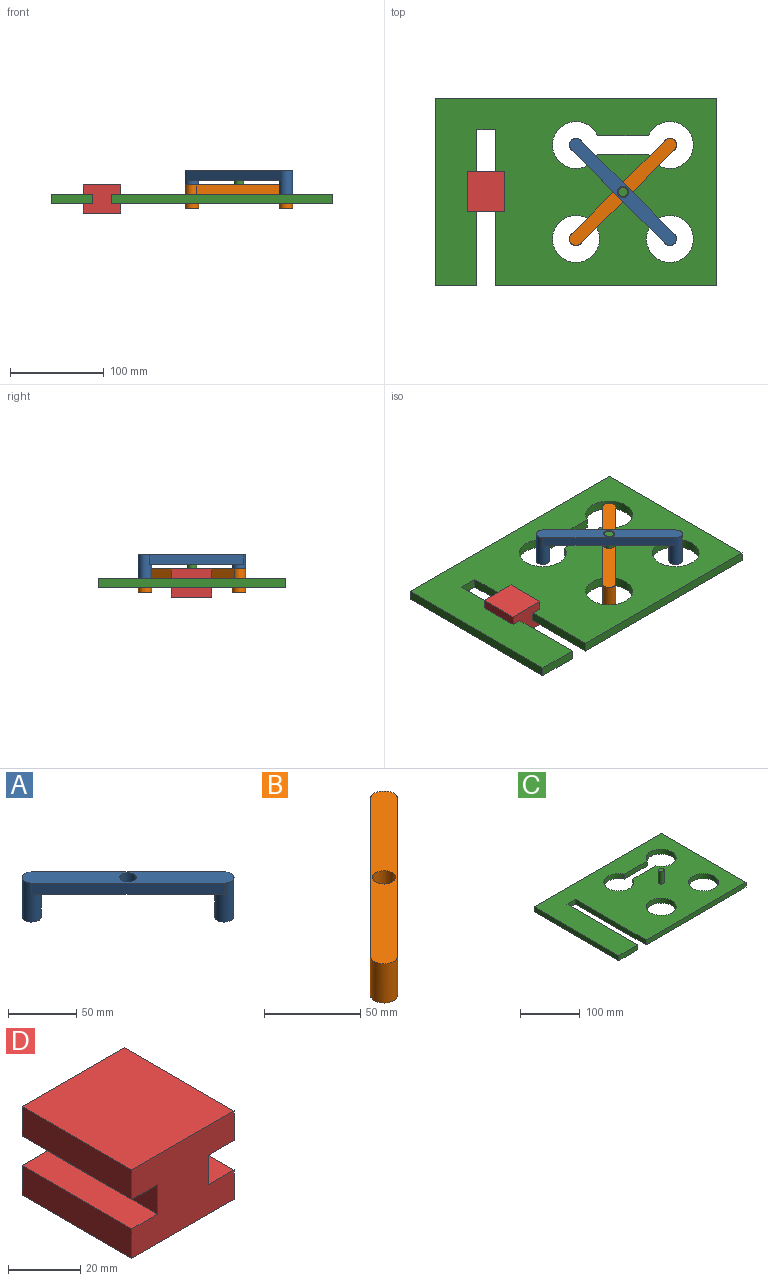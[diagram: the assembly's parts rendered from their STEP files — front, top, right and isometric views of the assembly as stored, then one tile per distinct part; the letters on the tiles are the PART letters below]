
ASSEMBLY  parts=4 mates=3
PART A: 9 faces, bbox 114.1x114.1x35 mm
  f0: cylinder r=7.07mm len=35mm, axis (0,0,1), area 1332.9mm2, adj f1,f3,f5,f6,f7
  f1: plane 100x100mm, normal (-0.71,-0.71,0), area 1414.2mm2, adj f0,f2,f5,f6
  f2: cylinder r=7.07mm len=35mm, axis (0,0,1), area 1332.9mm2, adj f1,f3,f5,f6,f8
  f3: plane 100x100mm, normal (0.71,0.71,0), area 1414.2mm2, adj f0,f2,f5,f6
  f4: cylinder r=6mm len=12mm, axis (0,0,1), area 377mm2, adj f5,f6
  f5: plane 110x110mm, normal (0,0,-1), area 1729.8mm2, adj f0,f1,f2,f3,f4
  f6: plane 114.14x114.14mm, normal (0,0,1), area 2044mm2, adj f0,f1,f2,f3,f4
  f7: plane 14.14x14.14mm, normal (0,0,-1), area 157.1mm2, adj f0
  f8: plane 14.14x14.14mm, normal (0,0,-1), area 157.1mm2, adj f2
PART B: 9 faces, bbox 114.1x114.1x25 mm
  f0: plane 110x110mm, normal (0,0,-1), area 1729.8mm2, adj f1,f2,f3,f4,f5
  f1: plane 100x100mm, normal (0.71,-0.71,0), area 1414.2mm2, adj f0,f2,f4,f6
  f2: cylinder r=7.07mm len=25mm, axis (0,0,-1), area 888.6mm2, adj f0,f1,f3,f6,f8
  f3: plane 100x100mm, normal (-0.71,0.71,0), area 1414.2mm2, adj f0,f2,f4,f6
  f4: cylinder r=7.07mm len=25mm, axis (0,0,-1), area 888.6mm2, adj f0,f1,f3,f6,f7
  f5: cylinder r=6mm len=12mm, axis (0,0,-1), area 377mm2, adj f0,f6
  f6: plane 114.14x114.14mm, normal (0,0,1), area 2044mm2, adj f1,f2,f3,f4,f5
  f7: plane 14.14x14.14mm, normal (0,0,-1), area 157.1mm2, adj f4
  f8: plane 14.14x14.14mm, normal (0,0,-1), area 157.1mm2, adj f2
PART C: 18 faces, bbox 300x200x35 mm
  f0: plane 166.53x10mm, normal (1,0,0), area 1665.3mm2, adj f1,f13,f14,f15
  f1: plane 20x10mm, normal (0,-1,0), area 200mm2, adj f0,f2,f14,f15
  f2: plane 166.53x10mm, normal (-1,0,0), area 1665.3mm2, adj f1,f3,f14,f15
  f3: plane 235.65x10mm, normal (0,-1,0), area 2356.5mm2, adj f2,f4,f14,f15
  f4: plane 200x10mm, normal (1,0,0), area 2000mm2, adj f3,f5,f14,f15
  f5: plane 300x10mm, normal (0,1,0), area 3000mm2, adj f4,f6,f14,f15
  f6: plane 200x10mm, normal (-1,0,0), area 2000mm2, adj f5,f13,f14,f15
  f7: plane 54.17x10mm, normal (0,1,0), area 541.7mm2, adj f8,f10,f14,f15
  f8: cylinder r=25mm len=50mm, axis (0,0,1), area 1365mm2, adj f7,f9,f14,f15
  f9: plane 54.17x10mm, normal (0,-1,0), area 541.7mm2, adj f8,f10,f14,f15
  f10: cylinder r=25mm len=50mm, axis (0,0,1), area 1365mm2, adj f7,f9,f14,f15
  f11: cylinder r=25mm len=50mm, axis (0,0,1), area 1570.8mm2, adj f14,f15
  f12: cylinder r=25mm len=50mm, axis (0,0,1), area 1570.8mm2, adj f14,f15
  f13: plane 44.35x10mm, normal (0,-1,0), area 443.5mm2, adj f0,f6,f14,f15
  f14: plane 300x200mm, normal (0,0,-1), area 47788.1mm2, adj f0,f1,f2,f3,f4,f5,f6,f7
  f15: plane 300x200mm, normal (0,0,1), area 47709.6mm2, adj f0,f1,f2,f3,f4,f5,f6,f7
  f16: cylinder r=5mm len=25mm, axis (0,0,-1), area 785.4mm2, adj f15,f17
  f17: plane 10x10mm, normal (0,0,1), area 78.5mm2, adj f16
PART D: 14 faces, bbox 40x43x30 mm
  f0: plane 43x10mm, normal (0,0,-1), area 430mm2, adj f1,f3,f6,f13
  f1: plane 43x10mm, normal (-1,0,0), area 430mm2, adj f0,f3,f4,f13
  f2: plane 43x10mm, normal (1,0,0), area 430mm2, adj f3,f4,f5,f13
  f3: plane 40x30mm, normal (0,1,0), area 1000mm2, adj f0,f1,f2,f4,f5,f6,f7,f8
  f4: plane 43x40mm, normal (0,0,1), area 1720mm2, adj f1,f2,f3,f13
  f5: plane 43x10mm, normal (0,0,-1), area 430mm2, adj f2,f3,f7,f13
  f6: plane 43x10mm, normal (-1,0,0), area 430mm2, adj f0,f3,f8,f13
  f7: plane 43x10mm, normal (1,0,0), area 430mm2, adj f3,f5,f12,f13
  f8: plane 43x10mm, normal (0,0,1), area 430mm2, adj f3,f6,f10,f13
  f9: plane 43x10mm, normal (1,0,0), area 430mm2, adj f3,f11,f12,f13
  f10: plane 43x10mm, normal (-1,0,0), area 430mm2, adj f3,f8,f11,f13
  f11: plane 43x40mm, normal (0,0,-1), area 1720mm2, adj f3,f9,f10,f13
  f12: plane 43x10mm, normal (0,0,1), area 430mm2, adj f3,f7,f9,f13
  f13: plane 40x30mm, normal (0,-1,0), area 1000mm2, adj f0,f1,f2,f4,f5,f6,f7,f8
PLACE A rot(axis=(0,0,1),180deg) t=(200,200,5)mm
PLACE B at identity
PLACE C at identity fixed
PLACE D t=(0,13.22,0)mm
MATE revolute A.f4 <-> C.f16  axis (0,0,1) through (100,100,25)mm
MATE slider D.f13 <-> C.f1  axis (0,-1,0) through (-45.65,79.22,-5)mm
MATE cylindrical C.f16 <-> B.f5  axis (0,0,1) through (100,100,0)mm
